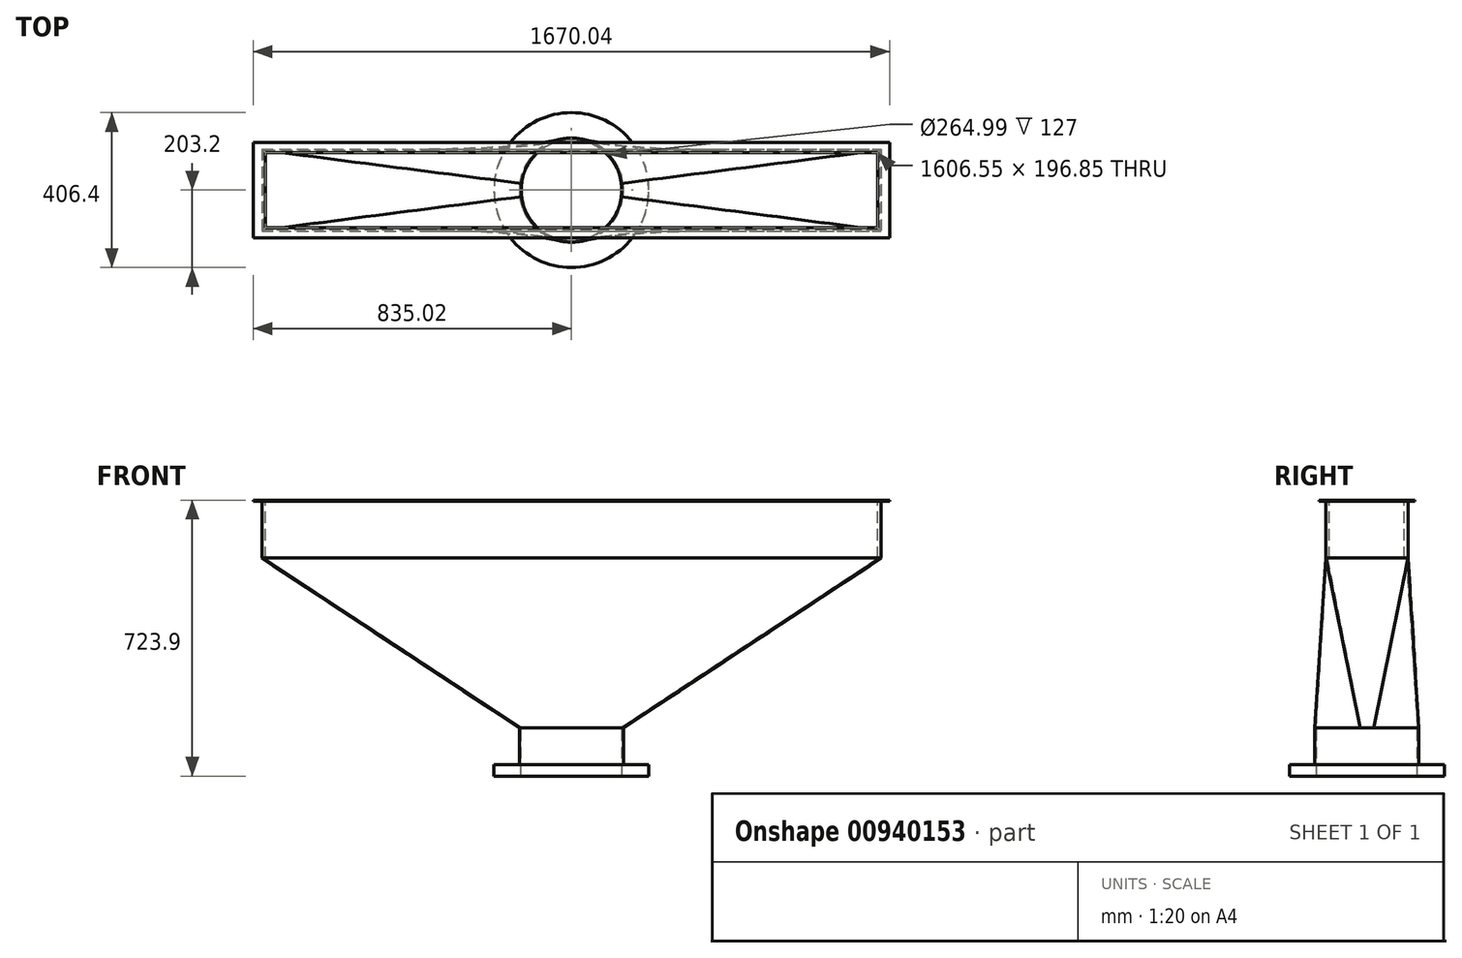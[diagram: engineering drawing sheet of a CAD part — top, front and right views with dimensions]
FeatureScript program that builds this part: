
annotation { "Feature Type Name" : "Feature", "Feature Type Description" : "" }
export const myFeature = defineFeature(function(context is Context, id is Id, definition is map)
    precondition{}
    {
        {
            var Q0;
            Q0=qCreatedBy(makeId("Top.planeOp"),FACE);
            cPlane(context, id + "F0", {"entities" : qUnion([Q0]), "cplaneType" : CPlaneType.OFFSET, "offset" : 723.9 * mm, "width" : 152.4 * mm, "height" : 152.4 * mm});
        }
        {
            var Q0;
            Q0=qCreatedBy(id+"F0.planeOp",FACE);
            var sketch = newSketch(context, id + "F1", { "sketchPlane" : qUnion([Q0])});
            skLineSegment(sketch, "E0.bottom", {"start": v(-835.03, -125.41) * mm, "end": v(835.03, -125.41) * mm});
            skLineSegment(sketch, "E0.top", {"start": v(-835.03, 125.41) * mm, "end": v(835.03, 125.41) * mm});
            skLineSegment(sketch, "E0.left", {"start": v(-835.03, -125.41) * mm, "end": v(-835.03, 125.41) * mm});
            skLineSegment(sketch, "E0.right", {"start": v(835.03, -125.41) * mm, "end": v(835.03, 125.41) * mm});
            skPoint(sketch, "E0.middle", {"position": v(0, 0) * mm});
            skLineSegment(sketch, "E1.bottom", {"start": v(803.28, -98.43) * mm, "end": v(-803.28, -98.43) * mm});
            skLineSegment(sketch, "E1.top", {"start": v(803.28, 98.43) * mm, "end": v(-803.28, 98.43) * mm});
            skLineSegment(sketch, "E1.left", {"start": v(803.28, -98.43) * mm, "end": v(803.28, 98.43) * mm});
            skLineSegment(sketch, "E1.right", {"start": v(-803.28, -98.43) * mm, "end": v(-803.28, 98.43) * mm});
            skSolve(sketch);
        }
        {
            var Q0;
            Q0 = qSketchRegion(id + "F1", true);
            extrude(context, id + "F2", {"entities" : qUnion([Q0]), "oppositeDirection" : true, "depth" : 2.67 * mm, "offsetDistance" : 25.4 * mm});
        }
        {
            var Q0;
            Q0=makeQuery(id+"F2.opExtrude","CAP_FACE",FACE,{"disambiguationData":[OSD([sQuery(id+"F1.wireOp",EDGE,"E0.bottom"),sQuery(id+"F1.wireOp",EDGE,"E0.top"),sQuery(id+"F1.wireOp",EDGE,"E0.left"),sQuery(id+"F1.wireOp",EDGE,"E0.right"),sQuery(id+"F1.wireOp",EDGE,"E1.bottom"),sQuery(id+"F1.wireOp",EDGE,"E1.top"),sQuery(id+"F1.wireOp",EDGE,"E1.left"),sQuery(id+"F1.wireOp",EDGE,"E1.right")])],"isStart":false});
            var sketch = newSketch(context, id + "F3", { "sketchPlane" : qUnion([Q0])});
            skLineSegment(sketch, "E2.bottom", {"start": v(-803.28, -98.43) * mm, "end": v(803.28, -98.43) * mm});
            skLineSegment(sketch, "E2.top", {"start": v(-803.28, 98.43) * mm, "end": v(803.28, 98.43) * mm});
            skLineSegment(sketch, "E2.left", {"start": v(-803.28, -98.43) * mm, "end": v(-803.28, 98.43) * mm});
            skLineSegment(sketch, "E2.right", {"start": v(803.28, -98.43) * mm, "end": v(803.28, 98.43) * mm});
            skPoint(sketch, "E2.middle", {"position": v(0, 0) * mm});
            skLineSegment(sketch, "E3.0", {"start": v(-812.3, 107.44) * mm, "end": v(812.3, 107.44) * mm});
            skLineSegment(sketch, "E3.1", {"start": v(-812.3, -107.44) * mm, "end": v(-812.3, 107.44) * mm});
            skLineSegment(sketch, "E3.2", {"start": v(-812.3, -107.44) * mm, "end": v(812.3, -107.44) * mm});
            skLineSegment(sketch, "E3.3", {"start": v(812.3, -107.44) * mm, "end": v(812.3, 107.44) * mm});
            skSolve(sketch);
        }
        {
            var Q0;
            Q0 = qSketchRegion(id + "F3", true);
            extrude(context, id + "F4", {"entities" : qUnion([Q0]), "operationType" : NewBodyOperationType.ADD, "depth" : 149.22 * mm, "offsetDistance" : 25.4 * mm});
        }
        {
            var Q0;
            Q0=qCreatedBy(makeId("Front.planeOp"),FACE);
            var sketch = newSketch(context, id + "F5", { "sketchPlane" : qUnion([Q0])});
            skLineSegment(sketch, "E4", {"start": v(0, 0) * mm, "end": v(203.2, 0) * mm, "construction": true});
            skLineSegment(sketch, "E5", {"start": v(203.2, 0) * mm, "end": v(203.2, 30.16) * mm});
            skLineSegment(sketch, "E6", {"start": v(203.2, 30.16) * mm, "end": v(136.53, 30.16) * mm});
            skLineSegment(sketch, "E7", {"start": v(136.53, 30.16) * mm, "end": v(136.53, 127) * mm});
            skLineSegment(sketch, "E8", {"start": v(136.53, 127) * mm, "end": v(132.5, 127) * mm});
            skLineSegment(sketch, "E9", {"start": v(132.5, 127) * mm, "end": v(132.5, 0) * mm});
            skLineSegment(sketch, "E10", {"start": v(132.5, 0) * mm, "end": v(203.2, 0) * mm});
            skLineSegment(sketch, "E11", {"start": v(0, 127) * mm, "end": v(0, 0) * mm, "construction": true});
            skLineSegment(sketch, "E12", {"start": v(132.5, 127) * mm, "end": v(803.28, 572) * mm, "construction": true});
            skSolve(sketch);
        }
        {
            var Q0;
            Q0 = qSketchRegion(id + "F5", true);
            var Q1;
            Q1=sQuery(id+"F5.wireOp",EDGE,"E11");
            revolve(context, id + "F6", {"surfaceOperationType" : NewSurfaceOperationType.NEW, "entities" : qUnion([Q0]), "axis" : qUnion([Q1]), "revolveType" : RevolveType.FULL});
        }
        {
            var Q0;
            Q0=makeQuery(id+"F4.opExtrude","CAP_FACE",FACE,{"disambiguationData":[OSD([sQuery(id+"F3.wireOp",EDGE,"E2.bottom"),sQuery(id+"F3.wireOp",EDGE,"E2.top"),sQuery(id+"F3.wireOp",EDGE,"E2.left"),sQuery(id+"F3.wireOp",EDGE,"E2.right"),sQuery(id+"F3.wireOp",EDGE,"E3.0"),sQuery(id+"F3.wireOp",EDGE,"E3.1"),sQuery(id+"F3.wireOp",EDGE,"E3.2"),sQuery(id+"F3.wireOp",EDGE,"E3.3")])],"isStart":false});
            var sketch = newSketch(context, id + "F7", { "sketchPlane" : qUnion([Q0])});
            skLineSegment(sketch, "E13.0", {"start": v(-812.3, -107.44) * mm, "end": v(-812.3, 107.44) * mm});
            skLineSegment(sketch, "E13.1", {"start": v(-812.3, -107.44) * mm, "end": v(812.3, -107.44) * mm});
            skLineSegment(sketch, "E13.2", {"start": v(812.3, -107.44) * mm, "end": v(812.3, 107.44) * mm});
            skLineSegment(sketch, "E13.3", {"start": v(-812.3, 107.44) * mm, "end": v(812.3, 107.44) * mm});
            skSolve(sketch);
        }
        {
            var Q0;
            Q0=makeQuery(id+"F6.opRevolve","SWEPT_FACE",FACE,{"disambiguationData":[OSD([sQuery(id+"F5.wireOp",EDGE,"E8")])]});
            var sketch = newSketch(context, id + "F8", { "sketchPlane" : qUnion([Q0])});
            skCircle(sketch, "E14.0", {"center": v(0, 0) * mm, "radius": 136.53 * mm});
            skSolve(sketch);
        }
        {
            var Q0;
            Q0=sQuery(id+"F5.wireOp",VERTEX,"E11.end");
            var Q1;
            Q1=sQuery(id+"F7.wireOp",VERTEX,"E13.0.end");
            var Q2;
            Q2=sQuery(id+"F7.wireOp",VERTEX,"E13.1.end");
            cPlane(context, id + "F9", {"entities" : qUnion([Q0, Q1, Q2]), "cplaneType" : CPlaneType.THREE_POINT, "offset" : 25.4 * mm, "width" : 152.4 * mm, "height" : 152.4 * mm});
        }
        {
            var Q0;
            Q0=sQuery(id+"F5.wireOp",VERTEX,"E11.end");
            var Q1;
            Q1=sQuery(id+"F7.wireOp",VERTEX,"E13.0.start");
            var Q2;
            Q2=sQuery(id+"F7.wireOp",VERTEX,"E13.2.end");
            cPlane(context, id + "F10", {"entities" : qUnion([Q0, Q1, Q2]), "cplaneType" : CPlaneType.THREE_POINT, "offset" : 25.4 * mm, "width" : 152.4 * mm, "height" : 152.4 * mm});
        }
        {
            var Q0;
            Q0=qCreatedBy(id+"F9.planeOp",FACE);
            var sketch = newSketch(context, id + "F11", { "sketchPlane" : qUnion([Q0])});
            skLineSegment(sketch, "E15", {"start": v(-819.37, 572) * mm, "end": v(-136.53, 127) * mm});
            skLineSegment(sketch, "E16", {"start": v(136.52, 127) * mm, "end": v(819.37, 572) * mm});
            skSolve(sketch);
        }
        {
            var Q0;
            Q0=qCreatedBy(id+"F10.planeOp",FACE);
            var sketch = newSketch(context, id + "F12", { "sketchPlane" : qUnion([Q0])});
            skLineSegment(sketch, "E17", {"start": v(-819.37, 572) * mm, "end": v(-136.52, 127) * mm});
            skLineSegment(sketch, "E18", {"start": v(136.53, 127) * mm, "end": v(819.37, 572) * mm});
            skSolve(sketch);
        }
        {
            var Q0;
            Q0 = qSketchRegion(id + "F7", true);
            var Q1;
            Q1 = qSketchRegion(id + "F8", true);
            var Q2;
            Q2=sQuery(id+"F12.wireOp",EDGE,"E18");
            var Q3;
            Q3=sQuery(id+"F11.wireOp",EDGE,"E16");
            var Q4;
            Q4=sQuery(id+"F11.wireOp",EDGE,"E15");
            var Q5;
            Q5=sQuery(id+"F12.wireOp",EDGE,"E17");
            loft(context, id + "F13", {"addGuides" : true, "sheetProfilesArray" : [{ "sheetProfileEntities" : qUnion([Q0]) }, { "sheetProfileEntities" : qUnion([Q1]) }], "guidesArray" : [{ "guideEntities" : qUnion([Q2]), "guideDerivativeType" : LoftGuideDerivativeType.DEFAULT, "guideDerivativeMagnitude" : 1 }, { "guideEntities" : qUnion([Q3]), "guideDerivativeType" : LoftGuideDerivativeType.DEFAULT, "guideDerivativeMagnitude" : 1 }, { "guideEntities" : qUnion([Q4]), "guideDerivativeType" : LoftGuideDerivativeType.DEFAULT, "guideDerivativeMagnitude" : 1 }, { "guideEntities" : qUnion([Q5]), "guideDerivativeType" : LoftGuideDerivativeType.DEFAULT, "guideDerivativeMagnitude" : 1 }]});
        }
        {
            var Q0;
            {var subQ0=makeQuery(id+"F8.imprint","IMPRINT",EDGE,{"derivedFrom":makeQuery(id+"F6.opRevolve","SWEPT_EDGE",EDGE,{"disambiguationData":[OSD([sQuery(id+"F5.wireOp",EDGE,"E8"),sQuery(id+"F5.wireOp",EDGE,"E9")])]})});Q0=makeQuery(id+"F13.opLoft","CAP_FACE",FACE,{"disambiguationData":[OSD([makeQuery(id+"F8.imprint","IMPRINT",FACE,{"disambiguationData":[TD([[makeQuery(id+"F8.imprint","IMPRINT",EDGE,{"derivedFrom":sQuery(id+"F8.wireOp",EDGE,"E14.0")}),1.0]])]}),makeQuery(id+"F8.imprint","IMPRINT",FACE,{"disambiguationData":[TD([[subQ0,1.0]])]})])],"isStart":true});}
            var Q1;
            {var subQ0=makeQuery(id+"F7.imprint","IMPRINT",EDGE,{"derivedFrom":makeQuery(id+"F4.opExtrude","CAP_EDGE",EDGE,{"disambiguationData":[OSD([sQuery(id+"F3.wireOp",EDGE,"E2.bottom")])],"isStart":false})});Q1=makeQuery(id+"F13.opLoft","CAP_FACE",FACE,{"disambiguationData":[OSD([makeQuery(id+"F7.imprint","IMPRINT",FACE,{"disambiguationData":[TD([[makeQuery(id+"F7.imprint","IMPRINT",EDGE,{"derivedFrom":sQuery(id+"F7.wireOp",EDGE,"E13.0")}),-1.0]])]}),makeQuery(id+"F7.imprint","IMPRINT",FACE,{"disambiguationData":[TD([[subQ0,-1.0]])]})])],"isStart":true});}
            shell(context, id + "F14", {"entities" : qUnion([Q0, Q1]), "thickness" : 2.67 * mm});
        }
        {
            var Q0;
            Q0=makeQuery(id+"F2.opExtrude","SWEPT_BODY",BODY,{"disambiguationData":[OSD([sQuery(id+"F1.wireOp",EDGE,"E0.bottom"),sQuery(id+"F1.wireOp",EDGE,"E0.top"),sQuery(id+"F1.wireOp",EDGE,"E0.left"),sQuery(id+"F1.wireOp",EDGE,"E0.right"),sQuery(id+"F1.wireOp",EDGE,"E1.bottom"),sQuery(id+"F1.wireOp",EDGE,"E1.top"),sQuery(id+"F1.wireOp",EDGE,"E1.left"),sQuery(id+"F1.wireOp",EDGE,"E1.right")])]});
            var Q1;
            Q1=makeQuery(id+"F13.opLoft","SWEPT_BODY",BODY,{"disambiguationData":[OSD([makeQuery(id+"F7.imprint","IMPRINT",FACE,{"disambiguationData":[TD([[makeQuery(id+"F7.imprint","IMPRINT",EDGE,{"derivedFrom":sQuery(id+"F7.wireOp",EDGE,"E13.0")}),-1.0]])]}),makeQuery(id+"F8.imprint","IMPRINT",FACE,{"disambiguationData":[TD([[makeQuery(id+"F8.imprint","IMPRINT",EDGE,{"derivedFrom":sQuery(id+"F8.wireOp",EDGE,"E14.0")}),1.0]])]}),sQuery(id+"F11.wireOp",EDGE,"E15"),sQuery(id+"F11.wireOp",EDGE,"E16"),sQuery(id+"F12.wireOp",EDGE,"E17"),sQuery(id+"F12.wireOp",EDGE,"E18")])]});
            var Q2;
            Q2=makeQuery(id+"F6.opRevolve","SWEPT_BODY",BODY,{"disambiguationData":[OSD([sQuery(id+"F5.wireOp",EDGE,"E5"),sQuery(id+"F5.wireOp",EDGE,"E6"),sQuery(id+"F5.wireOp",EDGE,"E7"),sQuery(id+"F5.wireOp",EDGE,"E8"),sQuery(id+"F5.wireOp",EDGE,"E9"),sQuery(id+"F5.wireOp",EDGE,"E10")])]});
            booleanBodies(context, id + "F15", {"operationType" : BooleanOperationType.UNION, "tools" : qUnion([Q0, Q1, Q2])});
        }
    });
